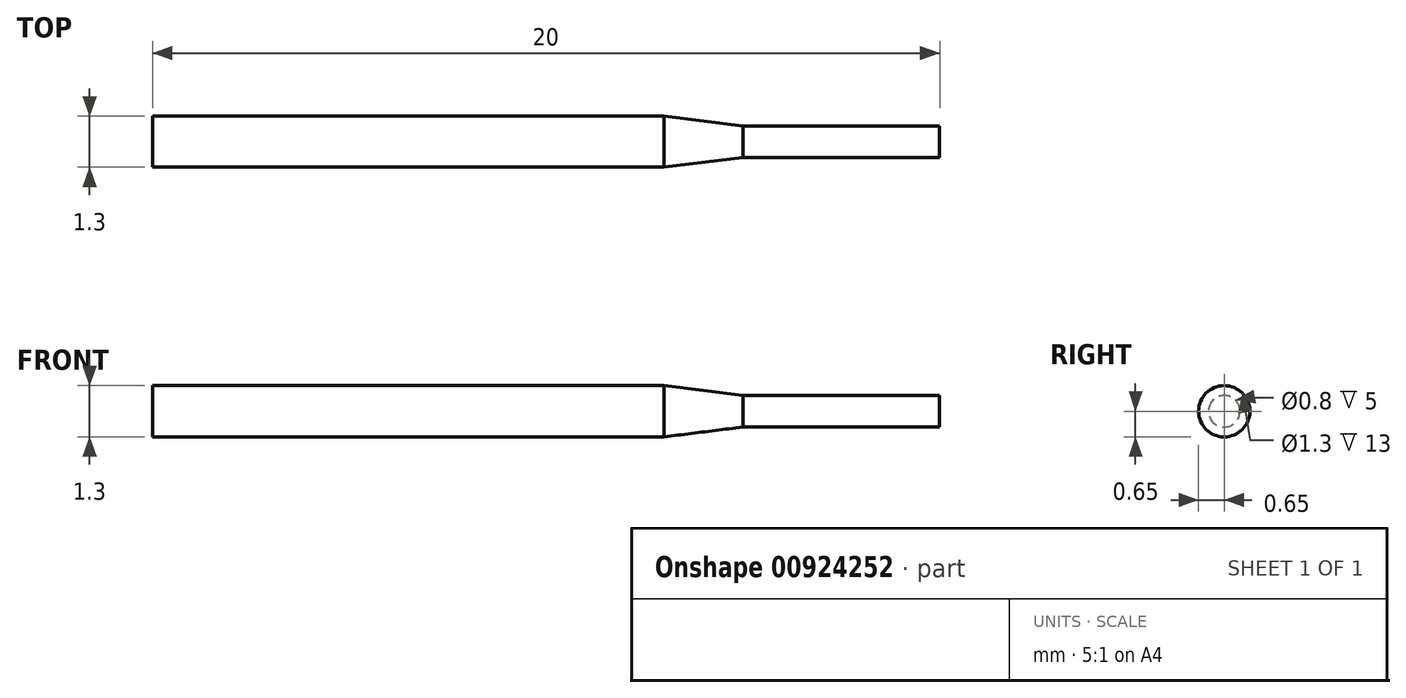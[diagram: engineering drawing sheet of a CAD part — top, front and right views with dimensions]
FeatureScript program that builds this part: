
annotation { "Feature Type Name" : "Feature", "Feature Type Description" : "" }
export const myFeature = defineFeature(function(context is Context, id is Id, definition is map)
    precondition{}
    {
        {
            var Q0;
            Q0=qCreatedBy(makeId("Top.planeOp"),FACE);
            var sketch = newSketch(context, id + "F0", { "sketchPlane" : qUnion([Q0])});
            skLineSegment(sketch, "E0", {"start": v(-3.61, 0) * mm, "end": v(3.87, 0) * mm, "construction": true});
            skLineSegment(sketch, "E1", {"start": v(-13.66, 0) * mm, "end": v(-13.66, 0.65) * mm});
            skLineSegment(sketch, "E2", {"start": v(-13.66, 0.65) * mm, "end": v(-0.66, 0.65) * mm});
            skLineSegment(sketch, "E3", {"start": v(-0.66, 0.65) * mm, "end": v(1.34, 0.4) * mm});
            skLineSegment(sketch, "E4", {"start": v(1.34, 0.4) * mm, "end": v(6.34, 0.4) * mm});
            skLineSegment(sketch, "E5", {"start": v(6.34, 0.4) * mm, "end": v(6.34, 0) * mm});
            skSolve(sketch);
        }
        {
            var Q0;
            Q0 = qSketchRegion(id + "F0", true);
            var Q1;
            Q1=sQuery(id+"F0.wireOp",EDGE,"E2");
            var Q2;
            Q2=sQuery(id+"F0.wireOp",EDGE,"E3");
            var Q3;
            Q3=sQuery(id+"F0.wireOp",EDGE,"E4");
            var Q4;
            Q4=sQuery(id+"F0.wireOp",EDGE,"E1");
            var Q5;
            Q5=sQuery(id+"F0.wireOp",EDGE,"E5");
            var Q6;
            Q6=sQuery(id+"F0.wireOp",EDGE,"E0");
            revolve(context, id + "F1", {"bodyType" : ToolBodyType.SURFACE, "surfaceOperationType" : NewSurfaceOperationType.NEW, "entities" : qUnion([Q0]), "surfaceEntities" : qUnion([Q1, Q2, Q3, Q4, Q5]), "axis" : qUnion([Q6]), "revolveType" : RevolveType.FULL});
        }
    });
